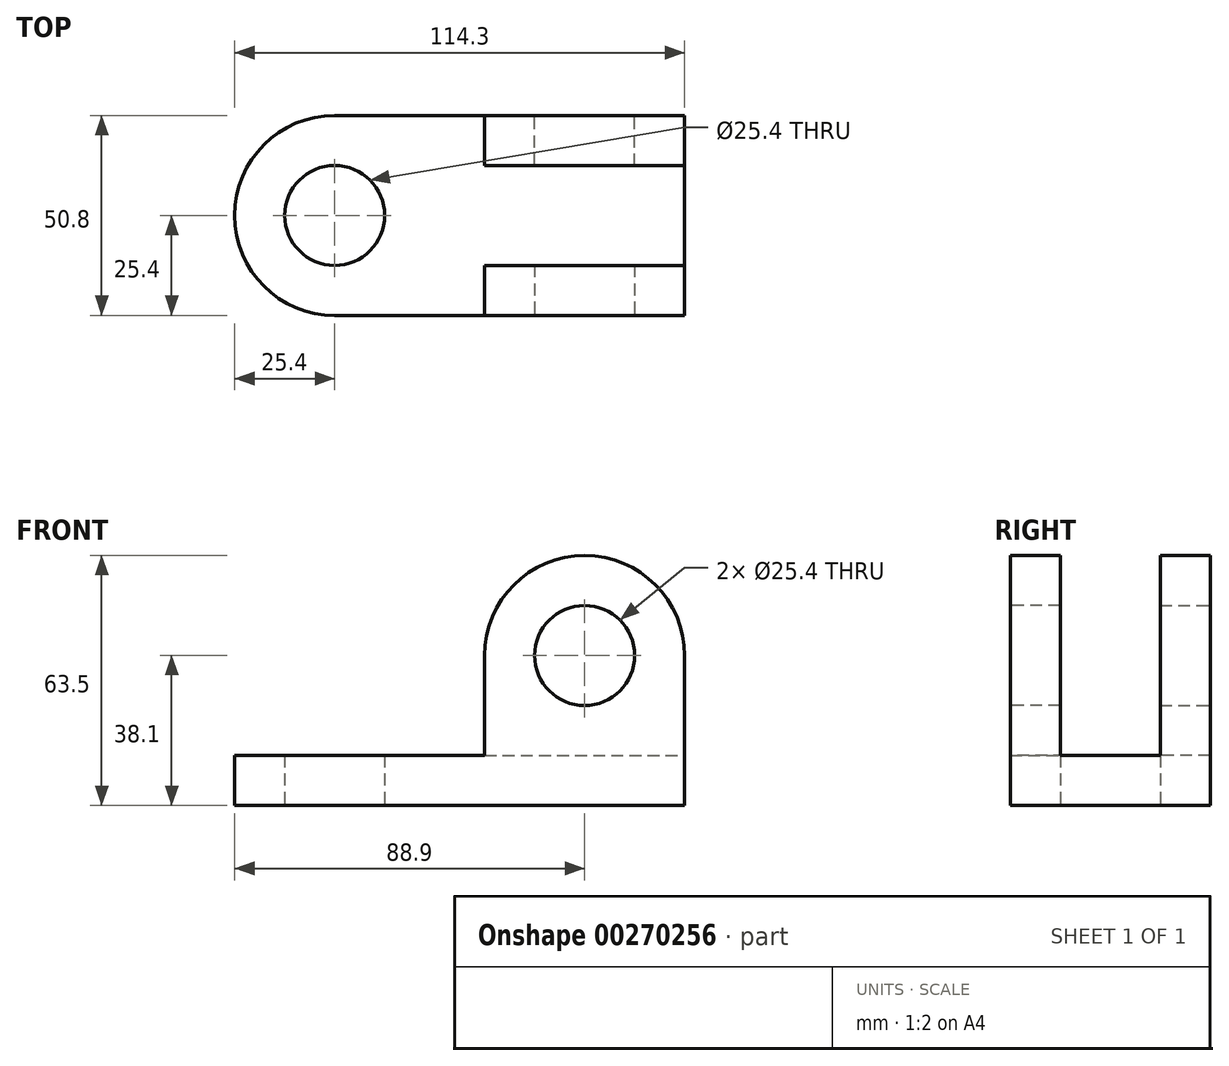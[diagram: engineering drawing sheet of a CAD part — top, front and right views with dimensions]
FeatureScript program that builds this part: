
annotation { "Feature Type Name" : "Feature", "Feature Type Description" : "" }
export const myFeature = defineFeature(function(context is Context, id is Id, definition is map)
    precondition{}
    {
        {
            var Q0;
            Q0=qCreatedBy(makeId("Top.planeOp"),FACE);
            var sketch = newSketch(context, id + "F0", { "sketchPlane" : qUnion([Q0])});
            skLineSegment(sketch, "E0.bottom", {"start": v(0, 0) * mm, "end": v(-88.9, 0) * mm});
            skLineSegment(sketch, "E0.top", {"start": v(0, 50.8) * mm, "end": v(-88.9, 50.8) * mm});
            skLineSegment(sketch, "E0.left", {"start": v(0, 0) * mm, "end": v(0, 50.8) * mm});
            skArc(sketch, "E1", {"start": v(-88.9, 50.8) * mm, "mid": v(-114.3, 25.4) * mm, "end": v(-88.9, 0) * mm});
            skCircle(sketch, "E2", {"center": v(-88.9, 25.4) * mm, "radius": 12.7 * mm});
            skSolve(sketch);
        }
        {
            var Q0;
            Q0 = qSketchRegion(id + "F0", true);
            extrude(context, id + "F1", {"entities" : qUnion([Q0]), "depth" : 12.7 * mm});
        }
        {
            var Q0;
            Q0=makeQuery(id+"F1.opExtrude","SWEPT_FACE",FACE,{"disambiguationData":[OSD([sQuery(id+"F0.wireOp",EDGE,"E0.bottom")])]});
            var sketch = newSketch(context, id + "F2", { "sketchPlane" : qUnion([Q0])});
            skLineSegment(sketch, "E3.bottom", {"start": v(0, 0) * mm, "end": v(-50.8, 0) * mm});
            skLineSegment(sketch, "E3.left", {"start": v(0, 0) * mm, "end": v(0, 38.1) * mm});
            skLineSegment(sketch, "E3.right", {"start": v(-50.8, 0) * mm, "end": v(-50.8, 38.1) * mm});
            skArc(sketch, "E4", {"start": v(0, 38.1) * mm, "mid": v(-25.4, 63.5) * mm, "end": v(-50.8, 38.1) * mm});
            skCircle(sketch, "E5", {"center": v(-25.4, 38.1) * mm, "radius": 12.7 * mm});
            skSolve(sketch);
        }
        {
            var Q0;
            Q0 = qSketchRegion(id + "F2", true);
            extrude(context, id + "F3", {"entities" : qUnion([Q0]), "operationType" : NewBodyOperationType.ADD, "oppositeDirection" : true, "depth" : 12.7 * mm});
        }
        {
            var Q0;
            Q0=makeQuery(id+"F1.opExtrude","SWEPT_FACE",FACE,{"disambiguationData":[OSD([sQuery(id+"F0.wireOp",EDGE,"E0.top")])]});
            var sketch = newSketch(context, id + "F4", { "sketchPlane" : qUnion([Q0])});
            skLineSegment(sketch, "E6.bottom", {"start": v(0, 0) * mm, "end": v(50.8, 0) * mm});
            skLineSegment(sketch, "E6.left", {"start": v(0, 0) * mm, "end": v(0, 38.1) * mm});
            skLineSegment(sketch, "E6.right", {"start": v(50.8, 0) * mm, "end": v(50.8, 38.1) * mm});
            skCircle(sketch, "E7", {"center": v(25.4, 38.1) * mm, "radius": 12.7 * mm});
            skArc(sketch, "E8", {"start": v(50.8, 38.1) * mm, "mid": v(25.4, 63.5) * mm, "end": v(0, 38.1) * mm});
            skSolve(sketch);
        }
        {
            var Q0;
            Q0 = qSketchRegion(id + "F4", true);
            extrude(context, id + "F5", {"entities" : qUnion([Q0]), "operationType" : NewBodyOperationType.ADD, "oppositeDirection" : true, "depth" : 12.7 * mm});
        }
    });
